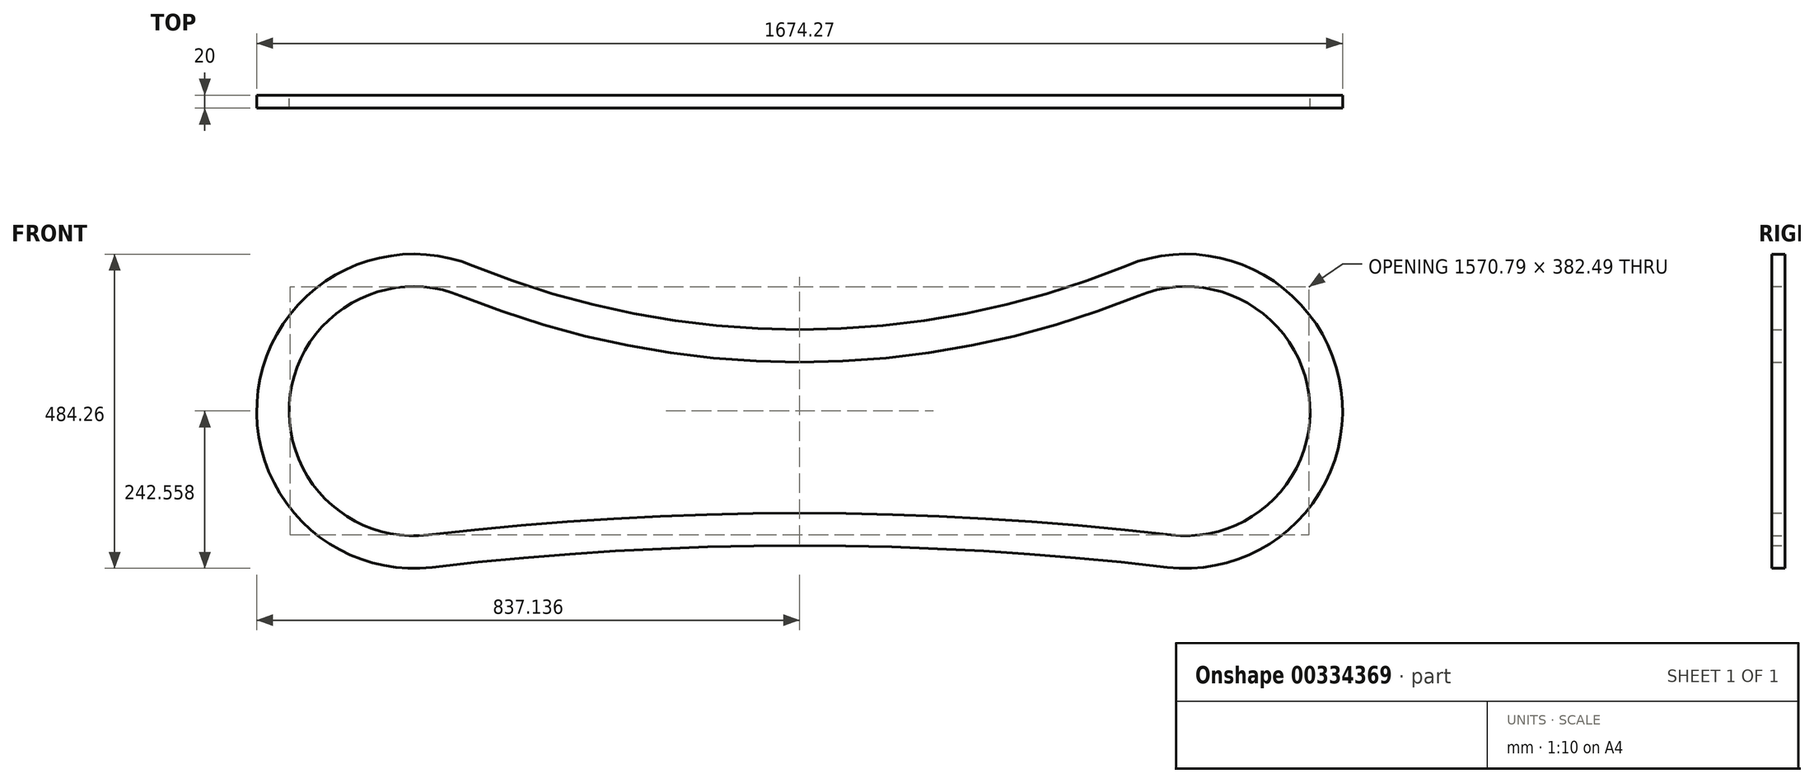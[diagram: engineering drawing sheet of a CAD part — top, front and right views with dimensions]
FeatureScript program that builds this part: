
annotation { "Feature Type Name" : "Feature", "Feature Type Description" : "" }
export const myFeature = defineFeature(function(context is Context, id is Id, definition is map)
    precondition{}
    {
        {
            var Q0;
            Q0=qCreatedBy(makeId("Front.planeOp"),FACE);
            var sketch = newSketch(context, id + "F0", { "sketchPlane" : qUnion([Q0])});
            skArc(sketch, "E0", {"start": v(-503.89, 224.27) * mm, "mid": v(-835.1, 32.51) * mm, "end": v(-566.86, -240.47) * mm});
            skArc(sketch, "E1", {"start": v(566.55, -240.47) * mm, "mid": v(834.79, 32.51) * mm, "end": v(503.58, 224.27) * mm});
            skLineSegment(sketch, "E2", {"start": v(-595.15, 0) * mm, "end": v(594.85, 0) * mm});
            skArc(sketch, "E3", {"start": v(566.55, -240.47) * mm, "mid": v(-0.15, -207.25) * mm, "end": v(-566.86, -240.47) * mm});
            skPoint(sketch, "E3.centerSnap0", {"position": v(-0.15, 0) * mm});
            skArc(sketch, "E4", {"start": v(-503.89, 224.27) * mm, "mid": v(-0.15, 125.7) * mm, "end": v(503.58, 224.27) * mm});
            skArc(sketch, "E5.0", {"start": v(-522.74, 177.96) * mm, "mid": v(-785.55, 25.8) * mm, "end": v(-572.7, -190.82) * mm});
            skArc(sketch, "E6.0", {"start": v(-522.74, 177.96) * mm, "mid": v(-0.15, 75.7) * mm, "end": v(522.43, 177.96) * mm});
            skArc(sketch, "E7.0", {"start": v(572.4, -190.82) * mm, "mid": v(785.24, 25.8) * mm, "end": v(522.43, 177.96) * mm});
            skArc(sketch, "E8.0", {"start": v(572.4, -190.82) * mm, "mid": v(-0.15, -157.25) * mm, "end": v(-572.7, -190.82) * mm});
            skSolve(sketch);
        }
        {
            var Q0;
            Q0=makeQuery(id+"F0.imprint","IMPRINT",FACE,{"disambiguationData":[TD([[makeQuery(id+"F0.imprint","IMPRINT",EDGE,{"derivedFrom":sQuery(id+"F0.wireOp",EDGE,"E0")}),1.0]])]});
            extrude(context, id + "F1", {"entities" : qUnion([Q0]), "depth" : 20 * mm});
        }
    });
